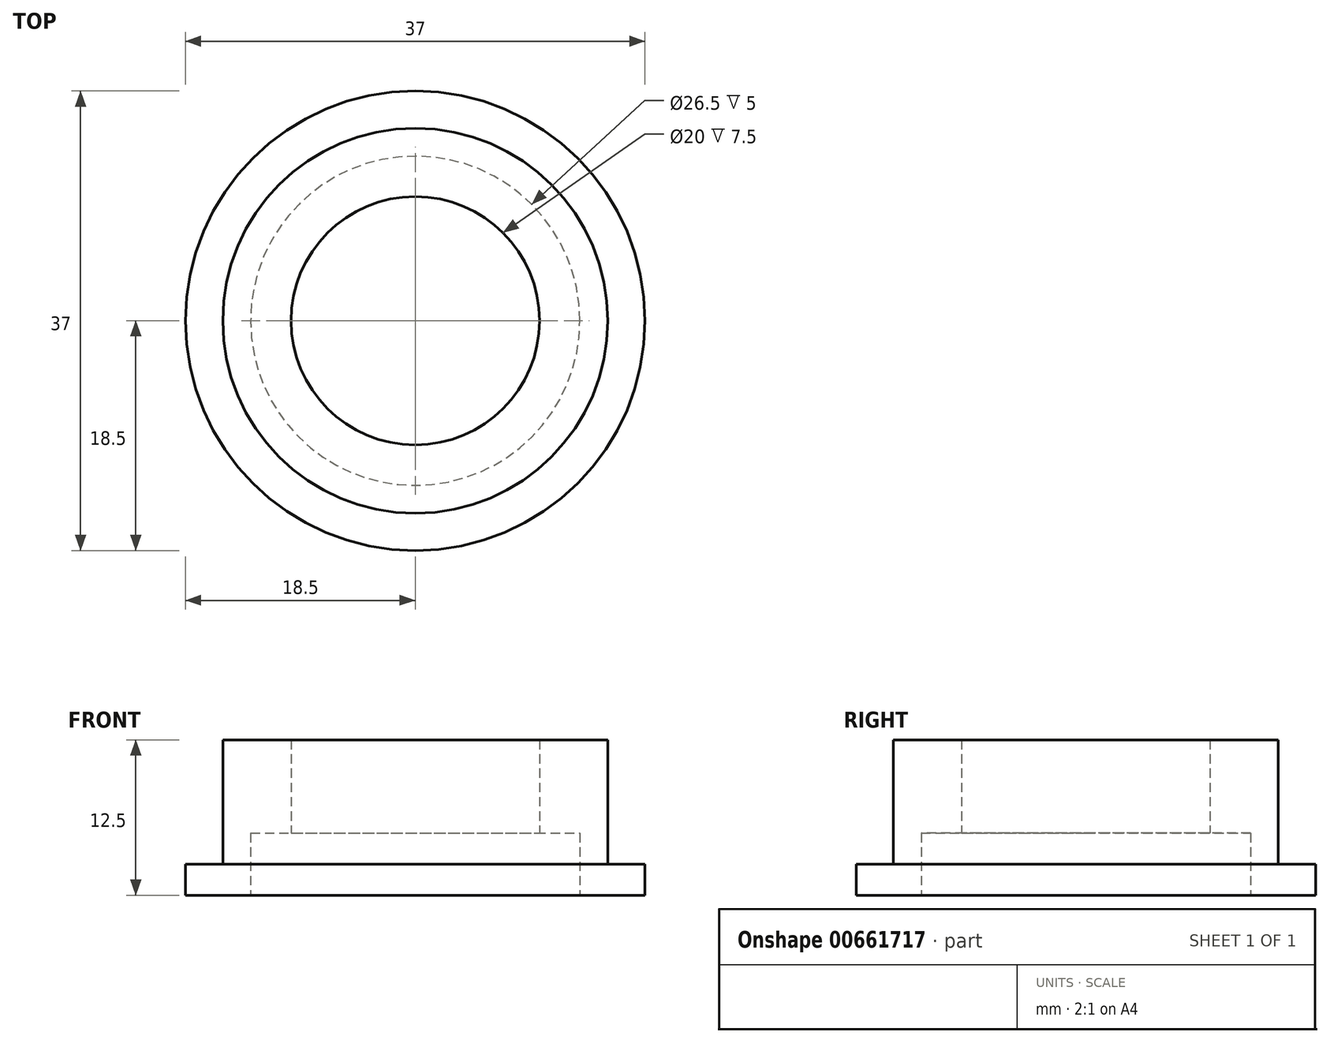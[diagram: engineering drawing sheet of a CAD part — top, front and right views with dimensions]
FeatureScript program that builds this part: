
annotation { "Feature Type Name" : "Feature", "Feature Type Description" : "" }
export const myFeature = defineFeature(function(context is Context, id is Id, definition is map)
    precondition{}
    {
        {
            var Q0;
            Q0=qCreatedBy(makeId("Top.planeOp"),FACE);
            var sketch = newSketch(context, id + "F0", { "sketchPlane" : qUnion([Q0])});
            skCircle(sketch, "E0", {"center": v(0, 0) * mm, "radius": 18.5 * mm});
            skSolve(sketch);
        }
        {
            var Q0;
            Q0=makeQuery(id+"F0.imprint","IMPRINT",FACE,{"disambiguationData":[TD([[makeQuery(id+"F0.imprint","IMPRINT",EDGE,{"derivedFrom":sQuery(id+"F0.wireOp",EDGE,"E0")}),1.0]])]});
            extrude(context, id + "F1", {"entities" : qUnion([Q0]), "depth" : 2.5 * mm, "offsetDistance" : 25 * mm});
        }
        {
            var Q0;
            Q0=makeQuery(id+"F1.opExtrude","CAP_FACE",FACE,{"disambiguationData":[OSD([sQuery(id+"F0.wireOp",EDGE,"E0")])],"isStart":false});
            var sketch = newSketch(context, id + "F2", { "sketchPlane" : qUnion([Q0])});
            skCircle(sketch, "E1", {"center": v(0, 0) * mm, "radius": 15.5 * mm});
            skSolve(sketch);
        }
        {
            var Q0;
            Q0=qSketchRegion(id+"F2",true);
            extrude(context, id + "F3", {"entities" : qUnion([Q0]), "operationType" : NewBodyOperationType.ADD, "depth" : 10 * mm, "offsetDistance" : 25 * mm});
        }
        {
            var Q0;
            Q0=makeQuery(id+"F1.opExtrude","CAP_FACE",FACE,{"disambiguationData":[OSD([sQuery(id+"F0.wireOp",EDGE,"E0")])],"isStart":true});
            var sketch = newSketch(context, id + "F4", { "sketchPlane" : qUnion([Q0])});
            skPoint(sketch, "E2.middle", {"position": v(0, 0) * mm});
            skCircle(sketch, "E3", {"center": v(0, 0) * mm, "radius": 13.25 * mm});
            skSolve(sketch);
        }
        {
            var Q0;
            Q0=makeQuery(id+"F4.imprint","IMPRINT",FACE,{"disambiguationData":[TD([[makeQuery(id+"F4.imprint","IMPRINT",EDGE,{"derivedFrom":sQuery(id+"F4.wireOp",EDGE,"E3")}),1.0]])]});
            var Q1;
            Q1=sQuery(id+"F4.wireOp",EDGE,"E3");
            extrude(context, id + "F5", {"entities" : qUnion([Q0]), "operationType" : NewBodyOperationType.REMOVE, "surfaceEntities" : qUnion([Q1]), "oppositeDirection" : true, "depth" : 5 * mm, "offsetDistance" : 25 * mm});
        }
        {
            var Q0;
            Q0=makeQuery(id+"F5.boolean.opBoolean","COPY",FACE,{"derivedFrom":makeQuery(id+"F5.opExtrude","CAP_FACE",FACE,{"disambiguationData":[OSD([sQuery(id+"F4.wireOp",EDGE,"E3")])],"isStart":false})});
            var sketch = newSketch(context, id + "F6", { "sketchPlane" : qUnion([Q0])});
            skCircle(sketch, "E4", {"center": v(0, 0) * mm, "radius": 10 * mm});
            skSolve(sketch);
        }
        {
            var Q0;
            Q0=makeQuery(id+"F6.imprint","IMPRINT",FACE,{"disambiguationData":[TD([[makeQuery(id+"F6.imprint","IMPRINT",EDGE,{"derivedFrom":sQuery(id+"F6.wireOp",EDGE,"E4")}),1.0]])]});
            extrude(context, id + "F7", {"entities" : qUnion([Q0]), "operationType" : NewBodyOperationType.REMOVE, "endBound" : BoundingType.THROUGH_ALL, "oppositeDirection" : true, "depth" : 25 * mm, "offsetDistance" : 25 * mm});
        }
    });
